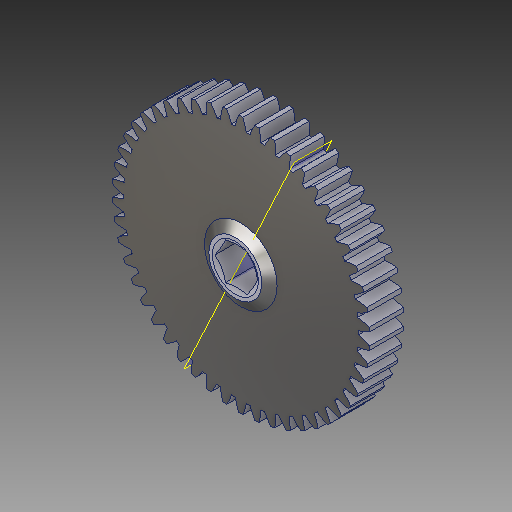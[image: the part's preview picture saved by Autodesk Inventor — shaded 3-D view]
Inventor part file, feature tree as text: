
AUTODESK INVENTOR PART (.ipt)
format: ipt  version: 2018 (Build 220112000, 112)  size: 476,672 bytes
history: native  units: in
note: dims shown in document units (in); Inventor stores cm internally (conversion verified against a paired STEP export)
features: plane x1, imported_body x1
ambient origin geometry x8: Origin, YZ Plane, XZ Plane, XY Plane, X Axis, Y Axis, Z Axis, Center Point
bodies: Solid1 (feature_tree)
feature tree (2):
  plane  "Work Plane2"
  imported_body  "Imported1"
